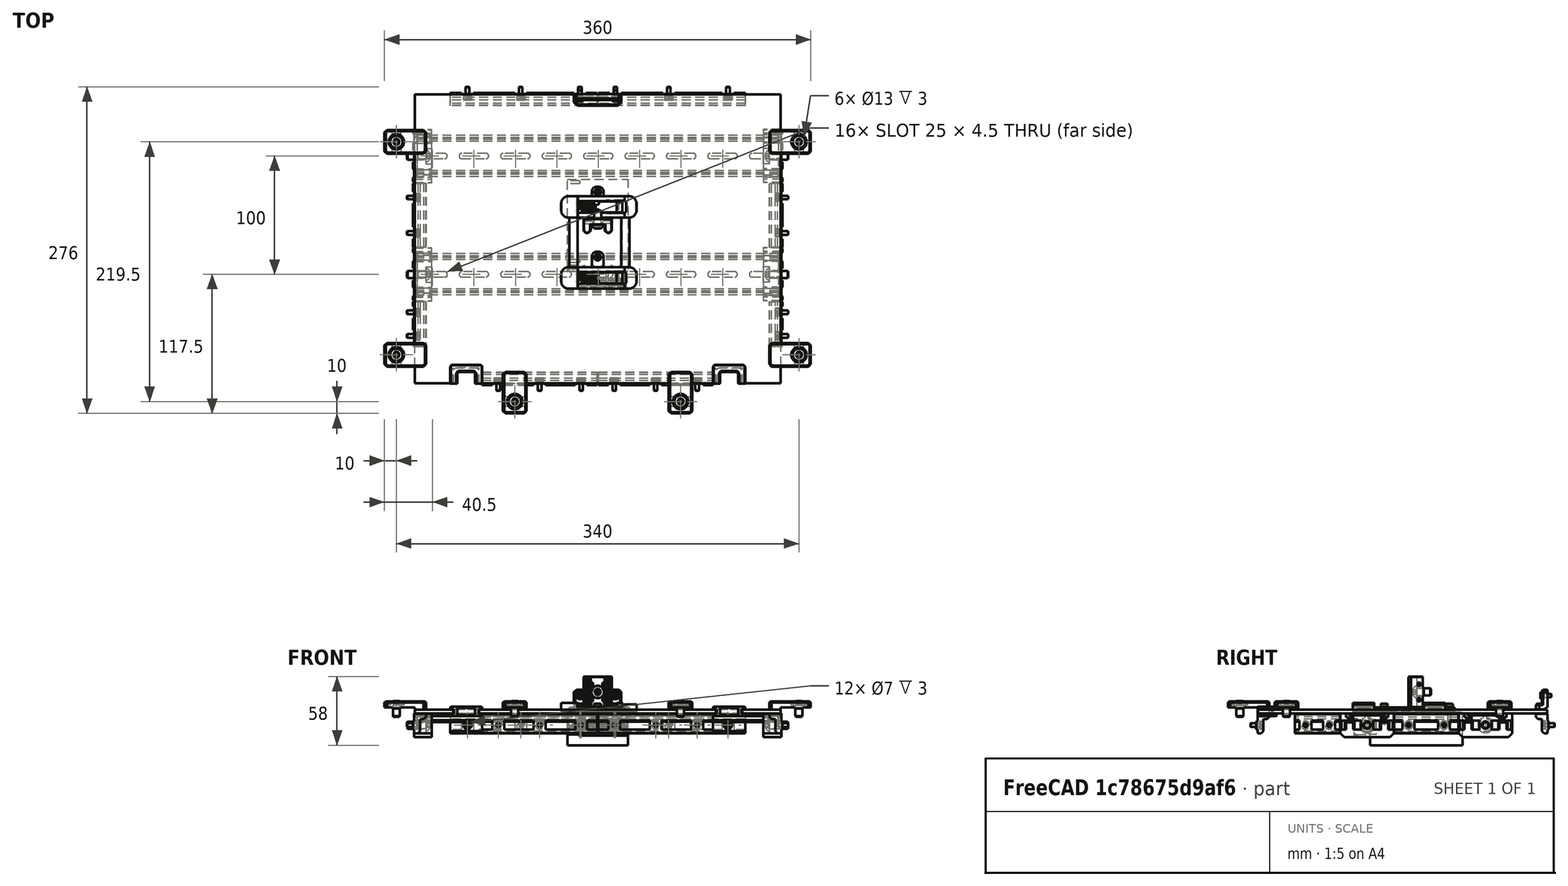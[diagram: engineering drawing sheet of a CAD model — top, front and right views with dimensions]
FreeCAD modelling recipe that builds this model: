
FCSTD DOCUMENT  (FreeCAD 0.19R24291 (Git))
Label: rear-bottom-panel-assembly
License: All rights reserved
LicenseURL: http://en.wikipedia.org/wiki/All_rights_reserved
objects: Part::FeaturePython×48, Part::Feature×28, App::Part×7, PartDesign::CoordinateSystem×1
note: 77 computed .brp shape members not serialized (recipe doc carries the construction recipe); baked Part::Feature solids carry a one-line shape summary decoded from their .brp

FEATURE [Part::FeaturePython] Screw105  label="M6x12-Screw"  # Fasteners workbench fastener (typed FeaturePython)
  Placement = pos=(0,0,13) rot=(1,0,0;1.5708rad)
  diameter = 4
  invert = true
  length = 1
  lengthCustom = 12
  matchOuter = true
  offset = 0
  thread = false
  type = 40
FEATURE [Part::Feature] Fusion017001001  label="5v-psu-mounter"
  Placement = pos=(0,0,0) rot=(0.707107,-0.707107,0;3.14159rad)
  shape: bbox 63.6 x 86 x 7.6 mm, 346 faces (baked)
FEATURE [Part::FeaturePython] Screw103  label="M3x6-Screw028"  # Fasteners workbench fastener (typed FeaturePython)
  Placement = pos=(-6e-15,-27.5,-1.6e-14) rot=(0,0,1;0rad)
  baseObject = -> Fusion017001001 [Edge438]
  diameter = 4
  invert = true
  length = 1
  lengthCustom = 6
  matchOuter = true
  offset = 0
  thread = false
  type = 34
FEATURE [Part::Feature] Fusion006002011004053036004001028003005006  label="RS-25-5-PSU"
  Placement = pos=(2.6e-14,-0.5,-4) rot=(0.57735,0.57735,-0.57735;4.18879rad)
  shape: bbox 51 x 91.75 x 28 mm, 292 faces (baked)
FEATURE [Part::FeaturePython] Screw106  label="M6x12-Screw001"  # Fasteners workbench fastener (typed FeaturePython)
  Placement = pos=(0,0,13) rot=(1,0,0;1.5708rad)
  diameter = 4
  invert = true
  length = 1
  lengthCustom = 12
  matchOuter = true
  offset = 0
  thread = false
  type = 40
FEATURE [Part::FeaturePython] Screw104  label="M3x6-Screw029"  # Fasteners workbench fastener (typed FeaturePython)
  Placement = pos=(6e-15,27.5,1.6e-14) rot=(0,0,1;0rad)
  baseObject = -> Fusion017001001 [Edge758]
  diameter = 4
  invert = true
  length = 1
  lengthCustom = 6
  matchOuter = true
  offset = 0
  thread = false
  type = 34
FEATURE [App::Part] Part050  label="5v-psu"
  Group = -> [Fusion006002011004053036004001028003005006,Fusion017001001,Screw103,Screw104]
  Origin = -> Origin050
  Placement = pos=(72,58.5,-13) rot=(0,0,-1;4.71239rad)
FEATURE [Part::Feature] Common001003002002001  label="din-309mm"
  Placement = pos=(0,-4,15) rot=(1,0,0;3.14159rad)
  shape: bbox 305 x 35 x 7.5 mm, 68 faces (baked)
FEATURE [Part::Feature] Chamfer002005  label="cable-hole-cover001"
  Placement = pos=(118.5,-134.5,-7.5) rot=(0,0.707107,0.707107;3.14159rad)
  shape: bbox 27 x 16 x 8 mm, 50 faces (baked)
FEATURE [Part::FeaturePython] Screw040  label="M3x8-Screw048"  # Fasteners workbench fastener (typed FeaturePython)
  Placement = pos=(153,-94,-15) rot=(0,-1,0;1.5708rad)
  diameter = 4
  invert = false
  length = 2
  lengthCustom = 8
  matchOuter = true
  offset = 0
  thread = false
  type = 34
FEATURE [Part::FeaturePython] Screw030  label="M3x8-Screw040"  # Fasteners workbench fastener (typed FeaturePython)
  Placement = pos=(14,-132.5,-15) rot=(-1,0,0;1.5708rad)
  diameter = 4
  invert = false
  length = 2
  lengthCustom = 8
  matchOuter = true
  offset = 0
  thread = false
  type = 34
FEATURE [Part::FeaturePython] Screw024  label="M3x8-Screw044"  # Fasteners workbench fastener (typed FeaturePython)
  Placement = pos=(-153,-94,-15) rot=(0,1,0;1.5708rad)
  diameter = 4
  invert = false
  length = 2
  lengthCustom = 8
  matchOuter = true
  offset = 0
  thread = false
  type = 34
FEATURE [Part::FeaturePython] Screw034  label="M3x8-Screw041"  # Fasteners workbench fastener (typed FeaturePython)
  Placement = pos=(84,-132.5,-15) rot=(-1,0,0;1.5708rad)
  diameter = 4
  invert = false
  length = 2
  lengthCustom = 8
  matchOuter = true
  offset = 0
  thread = false
  type = 34
FEATURE [PartDesign::CoordinateSystem] LCS_back_bottom_panel  label="LCS_back-bottom-panel"
  AttacherType = Attacher::AttachEngine3D
FEATURE [Part::FeaturePython] Screw025  label="M3x8-Screw045"  # Fasteners workbench fastener (typed FeaturePython)
  Placement = pos=(-153,-74,-15) rot=(0,1,0;1.5708rad)
  diameter = 4
  invert = false
  length = 2
  lengthCustom = 8
  matchOuter = true
  offset = 0
  thread = false
  type = 34
FEATURE [Part::FeaturePython] Screw016  label="M3x8-Screw053"  # Fasteners workbench fastener (typed FeaturePython)
  Placement = pos=(60,108.5,-15) rot=(1,0,0;1.5708rad)
  diameter = 4
  invert = false
  length = 2
  lengthCustom = 8
  matchOuter = true
  offset = 0
  thread = false
  type = 34
FEATURE [Part::FeaturePython] Screw011  label="M6x16-Screw006"  # Fasteners workbench fastener (typed FeaturePython)
  Placement = pos=(145,58,-15) rot=(0,-1,0;1.5708rad)
  diameter = 4
  invert = false
  length = 3
  lengthCustom = 16
  matchOuter = true
  offset = 0
  thread = false
  type = 40
FEATURE [Part::FeaturePython] Screw039  label="M3x8-Screw037"  # Fasteners workbench fastener (typed FeaturePython)
  Placement = pos=(-84,-132.5,-15) rot=(-1,0,0;1.5708rad)
  diameter = 4
  invert = false
  length = 2
  lengthCustom = 8
  matchOuter = true
  offset = 0
  thread = false
  type = 34
FEATURE [Part::FeaturePython] Screw036  label="M3x8-Screw043"  # Fasteners workbench fastener (typed FeaturePython)
  Placement = pos=(14,-132.5,-15) rot=(-1,0,0;1.5708rad)
  diameter = 4
  invert = false
  length = 2
  lengthCustom = 8
  matchOuter = true
  offset = 0
  thread = false
  type = 34
FEATURE [Part::FeaturePython] Screw041  label="M3x8-Screw049"  # Fasteners workbench fastener (typed FeaturePython)
  Placement = pos=(153,-74,-15) rot=(0,-1,0;1.5708rad)
  diameter = 4
  invert = false
  length = 2
  lengthCustom = 8
  matchOuter = true
  offset = 0
  thread = false
  type = 34
FEATURE [Part::FeaturePython] Screw033  label="M3x8-Screw034"  # Fasteners workbench fastener (typed FeaturePython)
  Placement = pos=(-84,-132.5,-15) rot=(-1,0,0;1.5708rad)
  diameter = 4
  invert = false
  length = 2
  lengthCustom = 8
  matchOuter = true
  offset = 0
  thread = false
  type = 34
FEATURE [Part::FeaturePython] Screw031  label="M3x8-Screw032"  # Fasteners workbench fastener (typed FeaturePython)
  Placement = pos=(-14,-132.5,-15) rot=(-1,0,0;1.5708rad)
  diameter = 4
  invert = false
  length = 2
  lengthCustom = 8
  matchOuter = true
  offset = 0
  thread = false
  type = 34
FEATURE [Part::FeaturePython] Screw037  label="M3x8-Screw035"  # Fasteners workbench fastener (typed FeaturePython)
  Placement = pos=(-14,-132.5,-15) rot=(-1,0,0;1.5708rad)
  diameter = 4
  invert = false
  length = 2
  lengthCustom = 8
  matchOuter = true
  offset = 0
  thread = false
  type = 34
FEATURE [Part::FeaturePython] Screw026  label="M3x8-Screw046"  # Fasteners workbench fastener (typed FeaturePython)
  Placement = pos=(-153,-7,-15) rot=(0,1,0;1.5708rad)
  diameter = 4
  invert = false
  length = 2
  lengthCustom = 8
  matchOuter = true
  offset = 0
  thread = false
  type = 34
FEATURE [Part::FeaturePython] Screw018  label="M3x8-Screw060"  # Fasteners workbench fastener (typed FeaturePython)
  Placement = pos=(-110,108.5,-15) rot=(1,0,0;1.5708rad)
  diameter = 4
  invert = false
  length = 2
  lengthCustom = 8
  matchOuter = true
  offset = 0
  thread = false
  type = 34
FEATURE [Part::FeaturePython] Screw022  label="M3x8-Screw056"  # Fasteners workbench fastener (typed FeaturePython)
  Placement = pos=(60,108.5,-15) rot=(1,0,0;1.5708rad)
  diameter = 4
  invert = false
  length = 2
  lengthCustom = 8
  matchOuter = true
  offset = 0
  thread = false
  type = 34
FEATURE [Part::FeaturePython] Screw023  label="M3x8-Screw057"  # Fasteners workbench fastener (typed FeaturePython)
  Placement = pos=(110,108.5,-15) rot=(1,0,0;1.5708rad)
  diameter = 4
  invert = false
  length = 2
  lengthCustom = 8
  matchOuter = true
  offset = 0
  thread = false
  type = 34
FEATURE [Part::FeaturePython] Screw029  label="M3x8-Screw039"  # Fasteners workbench fastener (typed FeaturePython)
  Placement = pos=(49,-132.5,-15) rot=(-1,0,0;1.5708rad)
  diameter = 4
  invert = false
  length = 2
  lengthCustom = 8
  matchOuter = true
  offset = 0
  thread = false
  type = 34
FEATURE [Part::FeaturePython] Screw020  label="M3x8-Screw062"  # Fasteners workbench fastener (typed FeaturePython)
  Placement = pos=(-15,108.5,-15) rot=(1,0,0;1.5708rad)
  diameter = 4
  invert = false
  length = 2
  lengthCustom = 8
  matchOuter = true
  offset = 0
  thread = false
  type = 34
FEATURE [Part::FeaturePython] Screw008  label="M6x16-Screw"  # Fasteners workbench fastener (typed FeaturePython)
  Placement = pos=(-145,-42,-15) rot=(0,1,0;1.5708rad)
  diameter = 4
  invert = false
  length = 3
  lengthCustom = 16
  matchOuter = true
  offset = 0
  thread = false
  type = 40
FEATURE [Part::FeaturePython] Screw017  label="M3x8-Screw054"  # Fasteners workbench fastener (typed FeaturePython)
  Placement = pos=(110,108.5,-15) rot=(1,0,0;1.5708rad)
  diameter = 4
  invert = false
  length = 2
  lengthCustom = 8
  matchOuter = true
  offset = 0
  thread = false
  type = 34
FEATURE [Part::FeaturePython] Screw012  label="M3x8-Screw"  # Fasteners workbench fastener (typed FeaturePython)
  Placement = pos=(-110,108.5,-15) rot=(1,0,0;1.5708rad)
  diameter = 4
  invert = false
  length = 2
  lengthCustom = 8
  matchOuter = true
  offset = 0
  thread = false
  type = 34
FEATURE [Part::FeaturePython] Screw014  label="M3x8-Screw059"  # Fasteners workbench fastener (typed FeaturePython)
  Placement = pos=(-15,108.5,-15) rot=(1,0,0;1.5708rad)
  diameter = 4
  invert = false
  length = 2
  lengthCustom = 8
  matchOuter = true
  offset = 0
  thread = false
  type = 34
FEATURE [Part::FeaturePython] Screw009  label="M6x16-Screw007"  # Fasteners workbench fastener (typed FeaturePython)
  Placement = pos=(-145,58,-15) rot=(0,1,0;1.5708rad)
  diameter = 4
  invert = false
  length = 3
  lengthCustom = 16
  matchOuter = true
  offset = 0
  thread = false
  type = 40
FEATURE [Part::FeaturePython] Screw006  label="M3x6-Screw"  # Fasteners workbench fastener (typed FeaturePython)
  Placement = pos=(15,107.5,10) rot=(1,0,0;1.5708rad)
  baseObject = -> Cut008004003004014002002005003004003002003001003001002001001 [Edge37]
  diameter = 4
  invert = false
  length = 1
  lengthCustom = 6
  matchOuter = true
  offset = 0
  thread = false
  type = 34
FEATURE [Part::FeaturePython] Screw004  label="M6x10-Screw014"  # Fasteners workbench fastener (typed FeaturePython)
  Placement = pos=(-170,-110,2) rot=(0,0,1;0rad)
  diameter = 4
  invert = true
  length = 0
  lengthCustom = 10
  matchOuter = true
  offset = 0
  thread = false
  type = 40
FEATURE [Part::FeaturePython] Screw003  label="M6x10-Screw013"  # Fasteners workbench fastener (typed FeaturePython)
  Placement = pos=(-70,-149.5,2) rot=(0,0,1;0rad)
  diameter = 4
  invert = true
  length = 0
  lengthCustom = 10
  matchOuter = true
  offset = 0
  thread = false
  type = 40
FEATURE [Part::FeaturePython] Screw005  label="M6x10-Screw015"  # Fasteners workbench fastener (typed FeaturePython)
  Placement = pos=(-170,70,2) rot=(0,0,1;0rad)
  diameter = 4
  invert = true
  length = 0
  lengthCustom = 10
  matchOuter = true
  offset = 0
  thread = false
  type = 40
FEATURE [Part::FeaturePython] Screw042  label="M3x8-Screw050"  # Fasteners workbench fastener (typed FeaturePython)
  Placement = pos=(153,-7,-15) rot=(0,-1,0;1.5708rad)
  diameter = 4
  invert = false
  length = 2
  lengthCustom = 8
  matchOuter = true
  offset = 0
  thread = false
  type = 34
FEATURE [Part::FeaturePython] Screw015  label="M3x8-Screw052"  # Fasteners workbench fastener (typed FeaturePython)
  Placement = pos=(15,108.5,-15) rot=(1,0,0;1.5708rad)
  diameter = 4
  invert = false
  length = 2
  lengthCustom = 8
  matchOuter = true
  offset = 0
  thread = false
  type = 34
FEATURE [Part::Feature] Chamfer002004  label="cable-hole-cover"
  Placement = pos=(-103.5,-134.5,-7.5) rot=(0,0.707107,0.707107;3.14159rad)
  shape: bbox 27 x 16 x 8 mm, 50 faces (baked)
FEATURE [Part::FeaturePython] Screw010  label="M6x16-Screw008"  # Fasteners workbench fastener (typed FeaturePython)
  Placement = pos=(145,-42,-15) rot=(0,-1,0;1.5708rad)
  diameter = 4
  invert = false
  length = 3
  lengthCustom = 16
  matchOuter = true
  offset = 0
  thread = false
  type = 40
FEATURE [Part::FeaturePython] Screw002  label="M6x10-Screw012"  # Fasteners workbench fastener (typed FeaturePython)
  Placement = pos=(70,-149.5,2) rot=(0,0,1;0rad)
  diameter = 4
  invert = true
  length = 0
  lengthCustom = 10
  matchOuter = true
  offset = 0
  thread = false
  type = 40
FEATURE [Part::FeaturePython] Screw019  label="M3x8-Screw061"  # Fasteners workbench fastener (typed FeaturePython)
  Placement = pos=(-65,108.5,-15) rot=(1,0,0;1.5708rad)
  diameter = 4
  invert = false
  length = 2
  lengthCustom = 8
  matchOuter = true
  offset = 0
  thread = false
  type = 34
FEATURE [Part::FeaturePython] Screw043  label="M3x8-Screw051"  # Fasteners workbench fastener (typed FeaturePython)
  Placement = pos=(153,23,-15) rot=(0,-1,0;1.5708rad)
  diameter = 4
  invert = false
  length = 2
  lengthCustom = 8
  matchOuter = true
  offset = 0
  thread = false
  type = 34
FEATURE [Part::FeaturePython] Screw032  label="M3x8-Screw033"  # Fasteners workbench fastener (typed FeaturePython)
  Placement = pos=(-49,-132.5,-15) rot=(-1,0,0;1.5708rad)
  diameter = 4
  invert = false
  length = 2
  lengthCustom = 8
  matchOuter = true
  offset = 0
  thread = false
  type = 34
FEATURE [Part::Feature] Common001003002002002  label="din-309mm001"
  Placement = pos=(0,96,15) rot=(1,0,0;3.14159rad)
  shape: bbox 305 x 35 x 7.5 mm, 68 faces (baked)
FEATURE [Part::FeaturePython] Screw038  label="M3x8-Screw036"  # Fasteners workbench fastener (typed FeaturePython)
  Placement = pos=(-49,-132.5,-15) rot=(-1,0,0;1.5708rad)
  diameter = 4
  invert = false
  length = 2
  lengthCustom = 8
  matchOuter = true
  offset = 0
  thread = false
  type = 34
FEATURE [Part::FeaturePython] Screw035  label="M3x8-Screw042"  # Fasteners workbench fastener (typed FeaturePython)
  Placement = pos=(49,-132.5,-15) rot=(-1,0,0;1.5708rad)
  diameter = 4
  invert = false
  length = 2
  lengthCustom = 8
  matchOuter = true
  offset = 0
  thread = false
  type = 34
FEATURE [Part::FeaturePython] Screw  label="M6x10-Screw"  # Fasteners workbench fastener (typed FeaturePython)
  Placement = pos=(170,70,2) rot=(0,0,1;0rad)
  diameter = 4
  invert = true
  length = 0
  lengthCustom = 10
  matchOuter = true
  offset = 0
  thread = false
  type = 40
FEATURE [Part::FeaturePython] Screw013  label="M3x8-Screw058"  # Fasteners workbench fastener (typed FeaturePython)
  Placement = pos=(-65,108.5,-15) rot=(1,0,0;1.5708rad)
  diameter = 4
  invert = false
  length = 2
  lengthCustom = 8
  matchOuter = true
  offset = 0
  thread = false
  type = 34
FEATURE [Part::FeaturePython] Screw027  label="M3x8-Screw047"  # Fasteners workbench fastener (typed FeaturePython)
  Placement = pos=(-153,23,-15) rot=(0,1,0;1.5708rad)
  diameter = 4
  invert = false
  length = 2
  lengthCustom = 8
  matchOuter = true
  offset = 0
  thread = false
  type = 34
FEATURE [Part::FeaturePython] Screw001  label="M6x10-Screw011"  # Fasteners workbench fastener (typed FeaturePython)
  Placement = pos=(170,-110,2) rot=(0,0,1;0rad)
  diameter = 4
  invert = true
  length = 0
  lengthCustom = 10
  matchOuter = true
  offset = 0
  thread = false
  type = 40
FEATURE [Part::FeaturePython] Screw007  label="M3x6-Screw001"  # Fasteners workbench fastener (typed FeaturePython)
  Placement = pos=(-15,107.5,10) rot=(1,0,0;1.5708rad)
  baseObject = -> Cut008004003004014002002005003004003002003001003001002001001 [Edge39]
  diameter = 4
  invert = false
  length = 1
  lengthCustom = 6
  matchOuter = true
  offset = 0
  thread = false
  type = 34
FEATURE [Part::FeaturePython] Screw021  label="M3x8-Screw055"  # Fasteners workbench fastener (typed FeaturePython)
  Placement = pos=(15,108.5,-15) rot=(1,0,0;1.5708rad)
  diameter = 4
  invert = false
  length = 2
  lengthCustom = 8
  matchOuter = true
  offset = 0
  thread = false
  type = 34
FEATURE [Part::FeaturePython] Screw028  label="M3x8-Screw038"  # Fasteners workbench fastener (typed FeaturePython)
  Placement = pos=(84,-132.5,-15) rot=(-1,0,0;1.5708rad)
  diameter = 4
  invert = false
  length = 2
  lengthCustom = 8
  matchOuter = true
  offset = 0
  thread = false
  type = 34
FEATURE [Part::Feature] Cut008004003004014002002005003004003002003001003001002001001  label="panel-support-bottom"
  Placement = pos=(2e-15,110.5,15) rot=(0,0.707107,-0.707107;3.14159rad)
  shape: bbox 40 x 10 x 16.5 mm, 30 faces (baked)
FEATURE [Part::Feature] Cut008004003004014002002005003004003002003001003001002001002002010001001  label="gasket-side-short002"
  Placement = pos=(-155,-84,-15) rot=(0.57735,-0.57735,0.57735;4.18879rad)
  shape: bbox 11 x 38 x 16.5 mm, 32 faces (baked)
FEATURE [Part::Feature] Cut008004003004014002002005003004003002003001003001002001002002009001001  label="gasket-side-long002"
  Placement = pos=(-155,8,-15) rot=(0.57735,-0.57735,0.57735;4.18879rad)
  shape: bbox 11 x 54 x 16.5 mm, 32 faces (baked)
FEATURE [Part::Feature] Cut008004003004014002002005003004003002003001003001002001002002008001001  label="gasket-bottom002"
  Placement = pos=(-65,110.5,-15) rot=(0,0.707107,-0.707107;3.14159rad)
  shape: bbox 124 x 11 x 16.5 mm, 40 faces (baked)
FEATURE [Part::Feature] Cut008004003004014002002005003004003002003001003001002001002002007001001  label="gasket-top002"
  Placement = pos=(-49,-134.5,-15) rot=(-1,0,0;1.5708rad)
  shape: bbox 97 x 11 x 16.5 mm, 40 faces (baked)
FEATURE [Part::Feature] Cut008004003004014002002005003004003002003001003001002001002002010001002  label="gasket-side-short003"
  Placement = pos=(155,-84,-15) rot=(0.57735,0.57735,-0.57735;4.18879rad)
  shape: bbox 11 x 38 x 16.5 mm, 32 faces (baked)
FEATURE [Part::Feature] Cut008004003004014002002005003004003002003001003001002001002002010001003  label="gasket-side-long003"
  Placement = pos=(155,8,-15) rot=(0.57735,0.57735,-0.57735;4.18879rad)
  shape: bbox 11 x 54 x 16.5 mm, 32 faces (baked)
FEATURE [Part::Feature] Cut008004003004014002002005003004003002003001003001002001002002010001004  label="gasket-bottom003"
  Placement = pos=(60,110.5,-15) rot=(0,0.707107,-0.707107;3.14159rad)
  shape: bbox 124 x 11 x 16.5 mm, 40 faces (baked)
FEATURE [Part::Feature] Cut008004003004014002002005003004003002003001003001002001002002010001005  label="gasket-top003"
  Placement = pos=(49,-134.5,-15) rot=(-1,0,0;1.5708rad)
  shape: bbox 97 x 11 x 16.5 mm, 40 faces (baked)
FEATURE [App::Part] Part001  label="outer-mount"
  Group = -> [Screw012,Screw013,Screw014,Screw015,Screw016,Screw017,Screw018,Screw019,Screw020,Screw021,Screw022,Screw023,Screw024,Screw025,Screw026,Screw027,Screw028,Screw029,Screw030,Screw031,Screw032,Screw033,Screw034,Screw035,Screw036,Screw037,Screw038,Screw039,Screw040,Screw041,Screw042,Screw043,Cut008004003004014002002005003004003002003001003001002001002002010001001,+7 more]
  Origin = -> Origin001
FEATURE [Part::Feature] Cut008004003004014002002005003004003002003001003001002001002002011001001  label="din-holder004"
  Placement = pos=(-155,58,-25) rot=(0,0,1;0rad)
  shape: bbox 16 x 45 x 20 mm, 59 faces (baked)
FEATURE [Part::Feature] Cut008004003004014002002005003004003002003001003001002001002002011001002  label="din-holder005"
  Placement = pos=(-155,-42,-25) rot=(0,0,1;0rad)
  shape: bbox 16 x 45 x 20 mm, 59 faces (baked)
FEATURE [Part::Feature] Cut008004003004014002002005003004003002003001003001002001002002011001003  label="din-holder006"
  Placement = pos=(155,58,-25) rot=(0,0,1;3.14159rad)
  shape: bbox 16 x 45 x 20 mm, 59 faces (baked)
FEATURE [Part::Feature] Cut008004003004014002002005003004003002003001003001002001002002011001004  label="din-holder007"
  Placement = pos=(155,-42,-25) rot=(0,0,1;3.14159rad)
  shape: bbox 16 x 45 x 20 mm, 59 faces (baked)
FEATURE [App::Part] Part002  label="din-mount"
  Group = -> [Common001003002002001,Common001003002002002,Screw008,Screw009,Screw010,Screw011,Cut008004003004014002002005003004003002003001003001002001002002011001001,Cut008004003004014002002005003004003002003001003001002001002002011001002,Cut008004003004014002002005003004003002003001003001002001002002011001003,Cut008004003004014002002005003004003002003001003001002001002002011001004]
  Origin = -> Origin002
FEATURE [Part::Feature] Body004001001  label="panel-support001"
  Placement = pos=(155,80,5) rot=(0,0.707107,-0.707107;3.14159rad)
  shape: bbox 35 x 20 x 7 mm, 31 faces (baked)
FEATURE [Part::Feature] Body004001002  label="panel-support002"
  Placement = pos=(155,-100,5) rot=(0,0.707107,-0.707107;3.14159rad)
  shape: bbox 35 x 20 x 7 mm, 31 faces (baked)
FEATURE [Part::Feature] Body004001003  label="panel-support003"
  Placement = pos=(-155,60,5) rot=(-1,0,0;1.5708rad)
  shape: bbox 35 x 20 x 7 mm, 31 faces (baked)
FEATURE [Part::Feature] Body004001004  label="panel-support004"
  Placement = pos=(-155,-120,5) rot=(-1,0,0;1.5708rad)
  shape: bbox 35 x 20 x 7 mm, 31 faces (baked)
FEATURE [Part::Feature] Body004001005  label="panel-support006"
  Placement = pos=(-60,-134.5,5) rot=(0.57735,0.57735,-0.57735;4.18879rad)
  shape: bbox 20 x 35 x 7 mm, 31 faces (baked)
FEATURE [Part::Feature] Body004001006  label="panel-support005"
  Placement = pos=(80,-134.5,5) rot=(0.57735,0.57735,-0.57735;4.18879rad)
  shape: bbox 20 x 35 x 7 mm, 31 faces (baked)
FEATURE [App::Part] Part  label="inner-mount"
  Group = -> [Cut008004003004014002002005003004003002003001003001002001001,Chamfer002004,Chamfer002005,Screw,Screw001,Screw002,Screw003,Screw004,Screw005,Screw007,Screw006,Body004001001,Body004001002,Body004001003,Body004001004,Body004001006,Body004001005]
  Origin = -> Origin
FEATURE [Part::Feature] Cut008001001  label="bottom-cable-mounter"
  shape: bbox 24 x 13 x 26 mm, 83 faces (baked)
FEATURE [App::Part] Part051  label="cable-mounter"
  Group = -> [Screw105,Cut008001001]
  Origin = -> Origin051
  Placement = pos=(120,138.5,-35) rot=(1,0,0;1.5708rad)
FEATURE [Part::Feature] Cut008004003004014002002005003004003002003001003001002001002002011001005
  shape: bbox 24 x 13 x 26 mm, 83 faces (baked)
FEATURE [App::Part] Part052  label="cable-mounter001"
  Group = -> [Screw106,Cut008004003004014002002005003004003002003001003001002001002002011001005]
  Origin = -> Origin052
  Placement = pos=(120,145.5,-2) rot=(1,0,0;3.14159rad)
FEATURE [Part::Feature] Cut008004003004014002002005003004003002003001003001002001002002011001007001001  label="panel-309x244mm"
  shape: bbox 309 x 244 x 3 mm, 14 faces (baked)
FEATURE [App::Part] Part003  label="rear-bottom-panel"
  Group = -> [Part,Part001,Part002,LCS_back_bottom_panel,Part050,Part051,Part052,Cut008004003004014002002005003004003002003001003001002001002002011001007001001]
  Origin = -> Origin003
